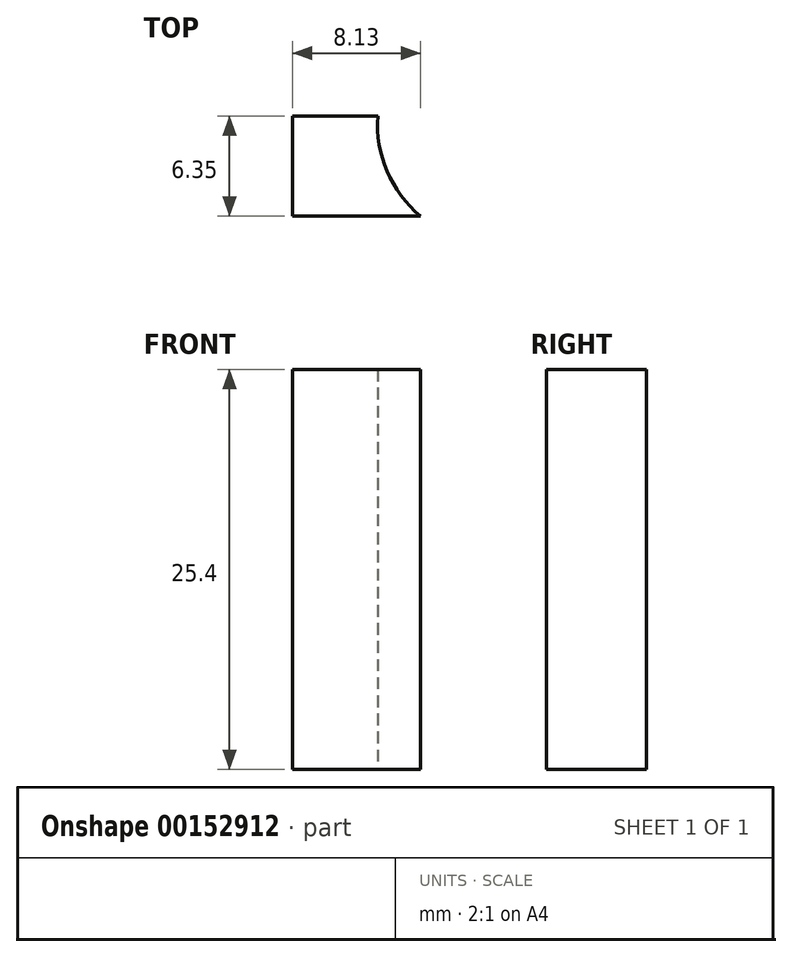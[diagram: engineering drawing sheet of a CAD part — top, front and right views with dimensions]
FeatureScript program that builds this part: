
annotation { "Feature Type Name" : "Feature", "Feature Type Description" : "" }
export const myFeature = defineFeature(function(context is Context, id is Id, definition is map)
    precondition{}
    {
        {
            var Q0;
            Q0=qCreatedBy(makeId("Top.planeOp"),FACE);
            var sketch = newSketch(context, id + "F0", { "sketchPlane" : qUnion([Q0])});
            skLineSegment(sketch, "E0.bottom", {"start": v(0, 0) * mm, "end": v(-5.42, 0) * mm});
            skLineSegment(sketch, "E0.top", {"start": v(2.71, -6.35) * mm, "end": v(-5.42, -6.35) * mm});
            skLineSegment(sketch, "E0.right", {"start": v(-5.42, 0) * mm, "end": v(-5.42, -6.35) * mm});
            skArc(sketch, "E1", {"start": v(0, 0) * mm, "mid": v(0.58, -3.5) * mm, "end": v(2.71, -6.35) * mm});
            skLineSegment(sketch, "E2", {"start": v(2.71, -6.35) * mm, "end": v(2.71, -8.06) * mm, "construction": true});
            skLineSegment(sketch, "E3", {"start": v(2.71, -8.06) * mm, "end": v(7.48, -8.06) * mm, "construction": true});
            skLineSegment(sketch, "E4", {"start": v(7.48, -0.56) * mm, "end": v(7.48, -8.06) * mm, "construction": true});
            skSolve(sketch);
        }
        {
            var Q0;
            Q0 = qSketchRegion(id + "F0", true);
            extrude(context, id + "F1", {"entities" : qUnion([Q0]), "depth" : 25.4 * mm});
        }
    });
